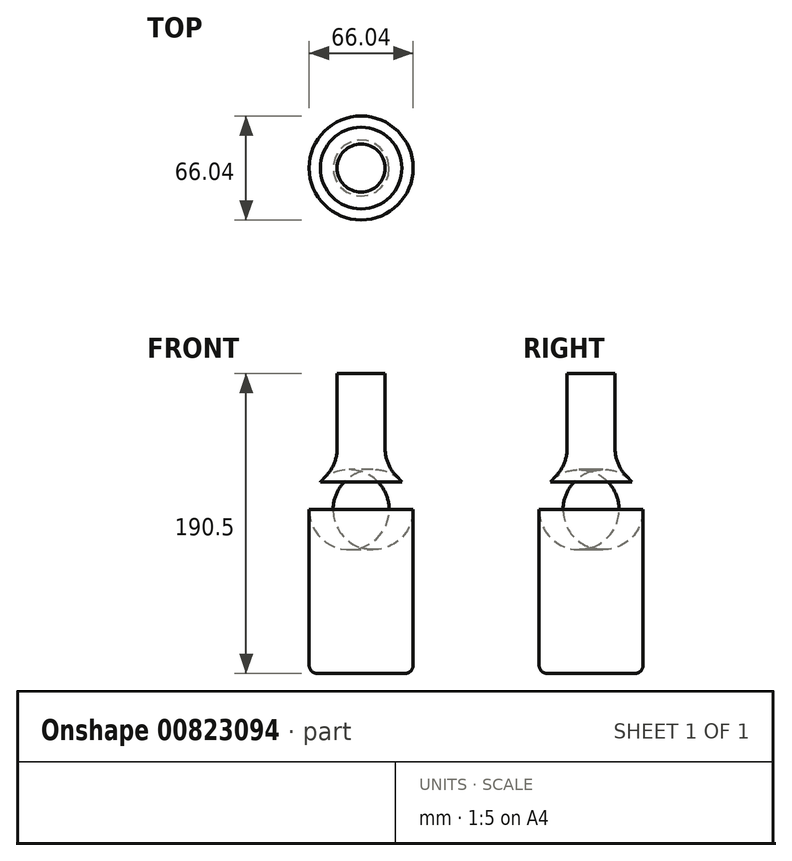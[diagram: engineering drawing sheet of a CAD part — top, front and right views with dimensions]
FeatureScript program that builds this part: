
annotation { "Feature Type Name" : "Feature", "Feature Type Description" : "" }
export const myFeature = defineFeature(function(context is Context, id is Id, definition is map)
    precondition{}
    {
        {
            var Q0;
            Q0=qCreatedBy(makeId("Front.planeOp"),FACE);
            var sketch = newSketch(context, id + "F0", { "sketchPlane" : qUnion([Q0])});
            skLineSegment(sketch, "E0", {"start": v(0, 95.25) * mm, "end": v(0, -95.25) * mm});
            skLineSegment(sketch, "E1", {"start": v(0, -95.25) * mm, "end": v(33.02, -95.25) * mm});
            skLineSegment(sketch, "E2", {"start": v(33.02, -95.25) * mm, "end": v(33.02, 19.05) * mm});
            skLineSegment(sketch, "E3", {"start": v(33.02, 19.05) * mm, "end": v(15.24, 37.5) * mm});
            skLineSegment(sketch, "E4", {"start": v(15.24, 37.5) * mm, "end": v(15.24, 95.25) * mm});
            skLineSegment(sketch, "E5", {"start": v(15.24, 95.25) * mm, "end": v(0, 95.25) * mm});
            skLineSegment(sketch, "E6", {"start": v(0, 149.97) * mm, "end": v(0, -145.34) * mm, "construction": true});
            skSolve(sketch);
        }
        {
            var Q0;
            Q0=qSketchRegion(id+"F0",true);
            var Q1;
            Q1=sQuery(id+"F0.wireOp",EDGE,"E6");
            revolve(context, id + "F1", {"surfaceOperationType" : NewSurfaceOperationType.NEW, "entities" : qUnion([Q0]), "axis" : qUnion([Q1]), "revolveType" : RevolveType.FULL});
        }
        {
            var Q0;
            Q0=makeQuery(id+"F1.opRevolve","SWEPT_EDGE",EDGE,{"disambiguationData":[OSD([sQuery(id+"F0.wireOp",EDGE,"E1"),sQuery(id+"F0.wireOp",EDGE,"E2")])]});
            fillet(context, id + "F2", {"entities" : qUnion([Q0]), "radius" : 5.08 * mm, "tangentPropagation" : true, "allowEdgeOverflow" : false});
        }
        {
            var Q0;
            Q0=makeQuery(id+"F1.opRevolve","SWEPT_EDGE",EDGE,{"disambiguationData":[OSD([sQuery(id+"F0.wireOp",EDGE,"E2"),sQuery(id+"F0.wireOp",EDGE,"E3")])]});
            var Q1;
            Q1=makeQuery(id+"F1.opRevolve","SWEPT_EDGE",EDGE,{"disambiguationData":[OSD([sQuery(id+"F0.wireOp",EDGE,"E3"),sQuery(id+"F0.wireOp",EDGE,"E4")])]});
            fillet(context, id + "F3", {"entities" : qUnion([Q0, Q1]), "radius" : 25.4 * mm, "tangentPropagation" : true, "allowEdgeOverflow" : false});
        }
    });
